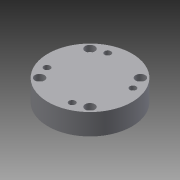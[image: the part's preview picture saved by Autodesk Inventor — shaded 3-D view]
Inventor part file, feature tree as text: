
AUTODESK INVENTOR PART (.ipt)
format: ipt  version: 2014 SP2 (Build 180246200, 246)  size: 260,608 bytes
history: native  units: in
note: dims shown in document units (in); Inventor stores cm internally (conversion verified against a paired STEP export)
features: other x273, sketch x9, hole x6, revolve x3, thread x1, pattern_linear x1
ambient origin geometry x8: Origin, YZ Plane, XZ Plane, XY Plane, X Axis, Y Axis, Z Axis, Center Point
bodies: Solid1 (feature_tree)
feature tree (293):
  revolve  "Revolution1"  Angle=360.0deg
  revolve  "Revolution2"  Angle=360.0deg
  thread  "Thread1"  [1 undecoded]
  revolve  "Revolution3"  [1 undecoded]
  hole  "Hole1"  [1 undecoded]
  hole  "Hole2"  [1 undecoded]
  hole  "Hole3"  [1 undecoded]
  hole  "Hole4"  [1 undecoded]
  hole  "Hole5"  [1 undecoded]
  hole  "Hole6"  [1 undecoded]
  pattern_linear  "Rectangular Pattern1"  [2 undecoded]
  other  "a1_XY"
  other  "a1_YZ"
  other  "a1_ZX"
  other  "a1_X"
  other  "a1_Y"
  other  "a1_Z"
  other  "a1_Center"
  other  "a2_XY"
  other  "a2_YZ"
  other  "a2_ZX"
  other  "a2_X"
  other  "a2_Y"
  other  "a2_Z"
  other  "a2_Center"
  other  "ar3_XY"
  other  "ar3_YZ"
  other  "ar3_ZX"
  other  "ar3_X"
  other  "ar3_Y"
  other  "ar3_Z"
  other  "ar3_Center"
  other  "ar4_XY"
  other  "ar4_YZ"
  other  "ar4_ZX"
  other  "ar4_X"
  other  "ar4_Y"
  other  "ar4_Z"
  other  "ar4_Center"
  other  "ar5_XY"
  other  "ar5_YZ"
  other  "ar5_ZX"
  other  "ar5_X"
  other  "ar5_Y"
  other  "ar5_Z"
  other  "ar5_Center"
  other  "ar6_XY"
  other  "ar6_YZ"
  other  "ar6_ZX"
  other  "ar6_X"
  other  "ar6_Y"
  other  "ar6_Z"
  other  "ar6_Center"
  other  "b1_XY"
  other  "b1_YZ"
  other  "b1_ZX"
  other  "b1_X"
  other  "b1_Y"
  other  "b1_Z"
  other  "b1_Center"
  other  "c11_XY"
  other  "c11_YZ"
  other  "c11_ZX"
  other  "c11_X"
  other  "c11_Y"
  other  "c11_Z"
  other  "c11_Center"
  other  "c22_XY"
  other  "c22_YZ"
  other  "c22_ZX"
  other  "c22_X"
  other  "c22_Y"
  other  "c22_Z"
  other  "c22_Center"
  other  "d11_XY"
  other  "d11_YZ"
  other  "d11_ZX"
  other  "d11_X"
  other  "d11_Y"
  other  "d11_Z"
  other  "d11_Center"
  other  "d22_XY"
  other  "d22_YZ"
  other  "d22_ZX"
  other  "d22_X"
  other  "d22_Y"
  other  "d22_Z"
  other  "d22_Center"
  other  "j_XY"
  other  "j_YZ"
  other  "j_ZX"
  other  "j_X"
  other  "j_Y"
  other  "j_Z"
  other  "j_Center"
  other  "k1_XY"
  other  "k1_YZ"
  other  "k1_ZX"
  other  "k1_X"
  other  "k1_Y"
  other  "k1_Z"
  other  "k1_Center"
  other  "k2_XY"
  other  "k2_YZ"
  other  "k2_ZX"
  other  "k2_X"
  other  "k2_Y"
  other  "k2_Z"
  other  "k2_Center"
  other  "po1_XY"
  other  "po1_YZ"
  other  "po1_ZX"
  other  "po1_X"
  other  "po1_Y"
  other  "po1_Z"
  other  "po1_Center"
  other  "po2_XY"
  other  "po2_YZ"
  other  "po2_ZX"
  other  "po2_X"
  other  "po2_Y"
  other  "po2_Z"
  other  "po2_Center"
  other  "po3_XY"
  other  "po3_YZ"
  other  "po3_ZX"
  other  "po3_X"
  other  "po3_Y"
  other  "po3_Z"
  other  "po3_Center"
  other  "r7_XY"
  other  "r7_YZ"
  other  "r7_ZX"
  other  "r7_X"
  other  "r7_Y"
  other  "r7_Z"
  other  "r7_Center"
  other  "r71_XY"
  other  "r71_YZ"
  other  "r71_ZX"
  other  "r71_X"
  other  "r71_Y"
  other  "r71_Z"
  other  "r71_Center"
  other  "r72_XY"
  other  "r72_YZ"
  other  "r72_ZX"
  other  "r72_X"
  other  "r72_Y"
  other  "r72_Z"
  other  "r72_Center"
  other  "r73_XY"
  other  "r73_YZ"
  other  "r73_ZX"
  other  "r73_X"
  other  "r73_Y"
  other  "r73_Z"
  other  "r73_Center"
  other  "rg_XY"
  other  "rg_YZ"
  other  "rg_ZX"
  other  "rg_X"
  other  "rg_Y"
  other  "rg_Z"
  other  "rg_Center"
  other  "rh_XY"
  other  "rh_YZ"
  other  "rh_ZX"
  other  "rh_X"
  other  "rh_Y"
  other  "rh_Z"
  other  "rh_Center"
  other  "rs_1_XY"
  other  "rs_1_YZ"
  other  "rs_1_ZX"
  other  "rs_1_X"
  other  "rs_1_Y"
  other  "rs_1_Z"
  other  "rs_1_Center"
  other  "rs_2_XY"
  other  "rs_2_YZ"
  other  "rs_2_ZX"
  other  "rs_2_X"
  other  "rs_2_Y"
  other  "rs_2_Z"
  other  "rs_2_Center"
  other  "rs_3_XY"
  other  "rs_3_YZ"
  other  "rs_3_ZX"
  other  "rs_3_X"
  other  "rs_3_Y"
  other  "rs_3_Z"
  other  "rs_3_Center"
  other  "rs_4_XY"
  other  "rs_4_YZ"
  other  "rs_4_ZX"
  other  "rs_4_X"
  other  "rs_4_Y"
  other  "rs_4_Z"
  other  "rs_4_Center"
  other  "sc1_XY"
  other  "sc1_YZ"
  other  "sc1_ZX"
  other  "sc1_X"
  other  "sc1_Y"
  other  "sc1_Z"
  other  "sc1_Center"
  other  "sc2_XY"
  other  "sc2_YZ"
  other  "sc2_ZX"
  other  "sc2_X"
  other  "sc2_Y"
  other  "sc2_Z"
  other  "sc2_Center"
  other  "sc3_XY"
  other  "sc3_YZ"
  other  "sc3_ZX"
  other  "sc3_X"
  other  "sc3_Y"
  other  "sc3_Z"
  other  "sc3_Center"
  other  "to_dummy_XY"
  other  "to_dummy_YZ"
  other  "to_dummy_ZX"
  other  "to_dummy_X"
  other  "to_dummy_Y"
  other  "to_dummy_Z"
  other  "to_dummy_Center"
  other  "to_nut_XY"
  other  "to_nut_YZ"
  other  "to_nut_ZX"
  other  "to_nut_X"
  other  "to_nut_Y"
  other  "to_nut_Z"
  other  "to_nut_Center"
  other  "to_rod_XY"
  other  "to_rod_YZ"
  other  "to_rod_ZX"
  other  "to_rod_X"
  other  "to_rod_Y"
  other  "to_rod_Z"
  other  "to_rod_Center"
  other  "to_tube_XY"
  other  "to_tube_YZ"
  other  "to_tube_ZX"
  other  "to_tube_X"
  other  "to_tube_Y"
  other  "to_tube_Z"
  other  "to_tube_Center"
  other  "to_wiper_XY"
  other  "to_wiper_YZ"
  other  "to_wiper_ZX"
  other  "to_wiper_X"
  other  "to_wiper_Y"
  other  "to_wiper_Z"
  other  "to_wiper_Center"
  other  "track1_XY"
  other  "track1_YZ"
  other  "track1_ZX"
  other  "track1_X"
  other  "track1_Y"
  other  "track1_Z"
  other  "track1_Center"
  other  "track2_XY"
  other  "track2_YZ"
  other  "track2_ZX"
  other  "track2_X"
  other  "track2_Y"
  other  "track2_Z"
  other  "track2_Center"
  other  "track3_XY"
  other  "track3_YZ"
  other  "track3_ZX"
  other  "track3_X"
  other  "track3_Y"
  other  "track3_Z"
  other  "track3_Center"
  other  "track4_XY"
  other  "track4_YZ"
  other  "track4_ZX"
  other  "track4_X"
  other  "track4_Y"
  other  "track4_Z"
  other  "track4_Center"
  sketch  "Sketch_1"  dims[d0=360.0deg d1=360.0deg]
  sketch  "Sketch_84"  dims[d40=0.104in d41=0.5in d42=0.15in d43=0.1in d44=0.5635in d45=0.5in d46=0.0in d47=0.7874in d49=1.1003in d50=0.7874in d52=1.1003in]
  sketch  "Sketch_85"  dims[d53=0.0in d54=0.0in d55=0.0in d56=0.0in d57=0.0in d58=0.0in d59=0.0in d60=0.0in d61=0.0in d62=0.0in d63=0.0in d64=0.0in d65=0.0in d66=0.0in d67=0.0in d68=0.0in d69=0.0in d70=0.0in d71=0.0in d72=0.0in d73=0.0in d74=0.0in d75=0.0in d76=0.0in d77=0.0in]
  sketch  "Sketch4"  dims[d2=0.3302in d3=0.0in d4=360.0deg]
  sketch  "Sketch5"  dims[d5=0.156in d6=0.75in d7=0.226in d8=0.148in d9=0.5635in d10=0.5in d11=0.0in]
  sketch  "Sketch6"  dims[d12=0.156in d13=0.75in d14=0.226in d15=0.148in d16=0.5635in d17=0.5in d18=0.0in]
  sketch  "Sketch7"  dims[d19=0.156in d20=0.75in d21=0.226in d22=0.148in d23=0.5635in d24=0.5in d25=0.0in]
  sketch  "Sketch8"  dims[d26=0.156in d27=0.75in d28=0.226in d29=0.148in d30=0.5635in d31=0.5in d32=0.0in]
  sketch  "Sketch9"  dims[d33=1.122in d34=0.75in d35=0.375in d36=0.25in d37=0.5635in d38=0.218in d39=0.0in]
note: 10 required parameter values undecoded (feature->parameter linkage not recoverable at this tier; creation-order binding heuristic only, values carry confidence <= 0.55)
